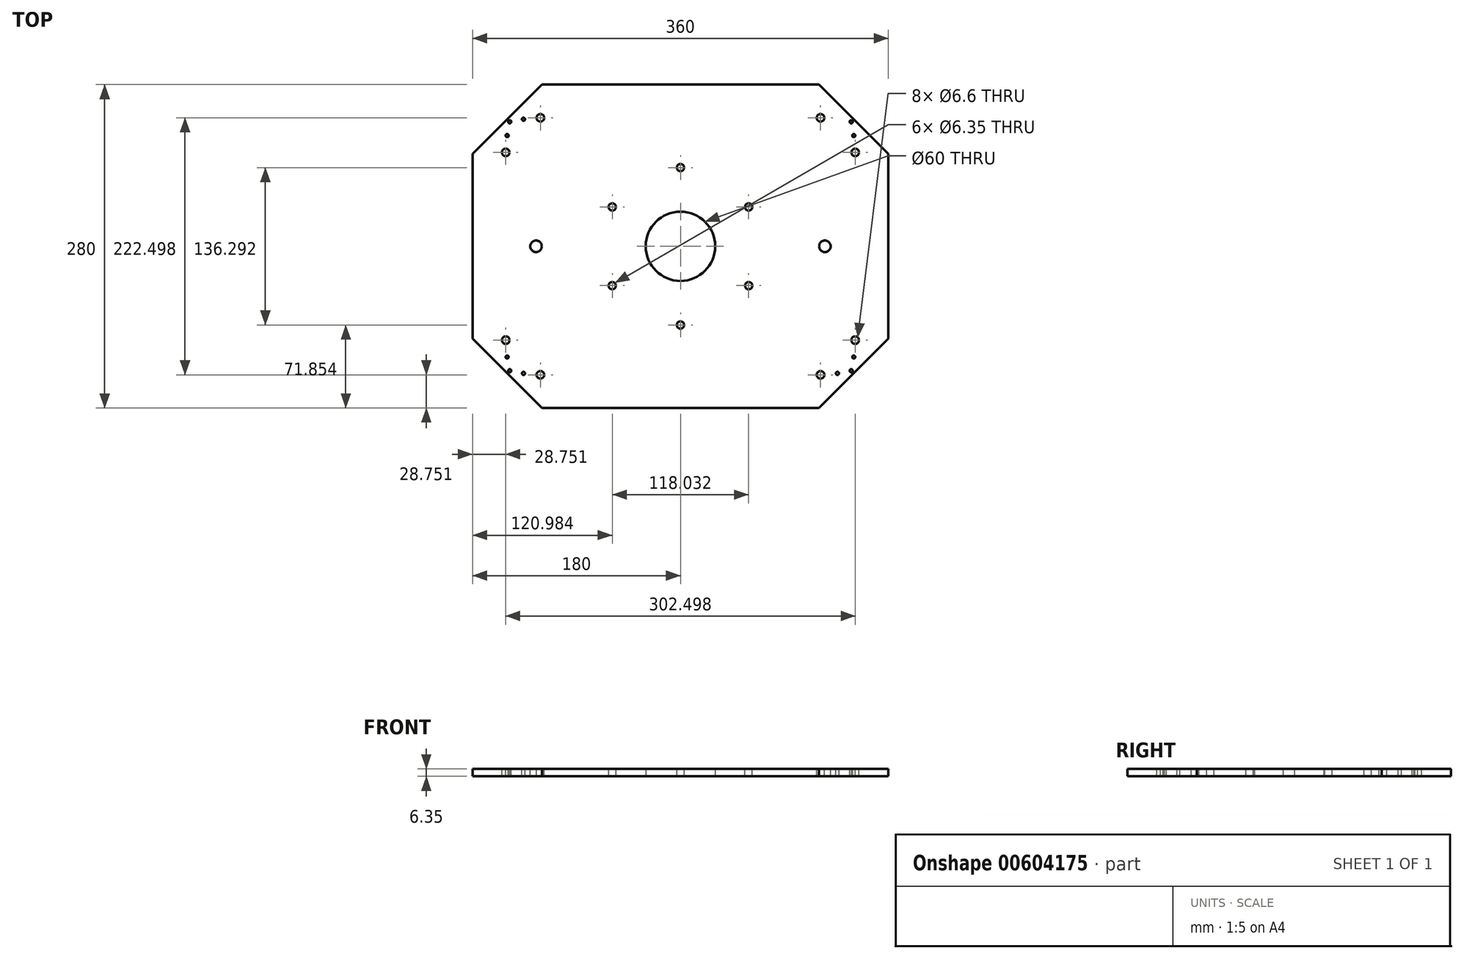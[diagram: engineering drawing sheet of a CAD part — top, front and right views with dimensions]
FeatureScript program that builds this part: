
annotation { "Feature Type Name" : "Feature", "Feature Type Description" : "" }
export const myFeature = defineFeature(function(context is Context, id is Id, definition is map)
    precondition{}
    {
        {
            var Q0;
            Q0=qCreatedBy(makeId("Top.planeOp"),FACE);
            var sketch = newSketch(context, id + "F0", { "sketchPlane" : qUnion([Q0])});
            skLineSegment(sketch, "E0", {"start": v(-120, 0) * mm, "end": v(-180, 60) * mm});
            skLineSegment(sketch, "E1", {"start": v(-180, 60) * mm, "end": v(-180, 220) * mm});
            skLineSegment(sketch, "E2", {"start": v(-180, 220) * mm, "end": v(-120, 280) * mm});
            skLineSegment(sketch, "E3", {"start": v(-120, 280) * mm, "end": v(120, 280) * mm});
            skLineSegment(sketch, "E4", {"start": v(120, 280) * mm, "end": v(180, 220) * mm});
            skLineSegment(sketch, "E5", {"start": v(180, 220) * mm, "end": v(180, 60) * mm});
            skLineSegment(sketch, "E6", {"start": v(180, 60) * mm, "end": v(120, 0) * mm});
            skLineSegment(sketch, "E7", {"start": v(120, 0) * mm, "end": v(-120, 0) * mm});
            skPoint(sketch, "E8.endSnap0", {"position": v(0, 280) * mm});
            skPoint(sketch, "E9.0.midPoint", {"position": v(0, 204.86) * mm});
            skPoint(sketch, "E10.0.midPoint", {"position": v(30.27, 157.38) * mm});
            skLineSegment(sketch, "E11", {"start": v(-180, 140) * mm, "end": v(180, 140) * mm, "construction": true});
            skLineSegment(sketch, "E12", {"start": v(0, 280) * mm, "end": v(0, 0) * mm, "construction": true});
            skCircle(sketch, "E13", {"center": v(0, 140) * mm, "radius": 30 * mm});
            skSolve(sketch);
        }
        {
            var Q0;
            Q0 = qSketchRegion(id + "F0", true);
            extrude(context, id + "F1", {"entities" : qUnion([Q0]), "depth" : 6.35 * mm, "offsetDistance" : 25 * mm});
        }
        {
            var Q0;
            {var subQ0=sQuery(id+"F0.wireOp",EDGE,"E2");var subQ1=sQuery(id+"F0.wireOp",EDGE,"E1");var subQ2=sQuery(id+"F0.wireOp",EDGE,"E3");var subQ3=sQuery(id+"F0.wireOp",EDGE,"E0");var subQ4=sQuery(id+"F0.wireOp",EDGE,"E4");var subQ5=sQuery(id+"F0.wireOp",EDGE,"E5");var subQ6=sQuery(id+"F0.wireOp",EDGE,"E6");var subQ7=sQuery(id+"F0.wireOp",EDGE,"E7");Q0=makeQuery(id+"FAH0EIdtt6uSNSP_1.boolean.opBoolean","SPLIT",FACE,{"disambiguationData":[TD([makeQuery(id+"F1.opExtrude","SWEPT_FACE",FACE,{"disambiguationData":[OSD([subQ3])]})])],"derivedFrom":makeQuery(id+"F1.opExtrude","CAP_FACE",FACE,{"disambiguationData":[OSD([subQ3,subQ1,subQ0,subQ2,subQ4,subQ5,subQ6,subQ7,sQuery(id+"F0.wireOp",EDGE,"E10.0"),sQuery(id+"F0.wireOp",EDGE,"E10.1"),sQuery(id+"F0.wireOp",EDGE,"E10.2"),sQuery(id+"F0.wireOp",EDGE,"E10.3"),sQuery(id+"F0.wireOp",EDGE,"E10.4"),sQuery(id+"F0.wireOp",EDGE,"E10.5")])],"isStart":false})});}
            var sketch = newSketch(context, id + "F2", { "sketchPlane" : qUnion([Q0])});
            skLineSegment(sketch, "E14", {"start": v(-180, 140) * mm, "end": v(180, 140) * mm, "construction": true});
            skPoint(sketch, "E15", {"position": v(0, 140) * mm});
            skPoint(sketch, "E16", {"position": v(-125, 140) * mm});
            skPoint(sketch, "E17", {"position": v(125, 140) * mm});
            skSolve(sketch);
        }
        {
            var Q0;
            Q0=sQuery(id+"F2.wireOp",VERTEX,"E16");
            var Q1;
            Q1=sQuery(id+"F2.wireOp",VERTEX,"E17");
            var Q2;
            Q2=makeQuery(id+"F1.opExtrude","SWEPT_BODY",BODY,{"disambiguationData":[OSD([sQuery(id+"F0.wireOp",EDGE,"E0"),sQuery(id+"F0.wireOp",EDGE,"E1"),sQuery(id+"F0.wireOp",EDGE,"E2"),sQuery(id+"F0.wireOp",EDGE,"E3"),sQuery(id+"F0.wireOp",EDGE,"E4"),sQuery(id+"F0.wireOp",EDGE,"E5"),sQuery(id+"F0.wireOp",EDGE,"E6"),sQuery(id+"F0.wireOp",EDGE,"E7"),sQuery(id+"F0.wireOp",EDGE,"E10.0"),sQuery(id+"F0.wireOp",EDGE,"E10.1"),sQuery(id+"F0.wireOp",EDGE,"E10.2"),sQuery(id+"F0.wireOp",EDGE,"E10.3"),sQuery(id+"F0.wireOp",EDGE,"E10.4"),sQuery(id+"F0.wireOp",EDGE,"E10.5")])]});
            hole(context, id + "F3", {"style" : HoleStyle.SIMPLE, "endStyle" : HoleEndStyle.THROUGH, "holeDiameter" : 10 * mm, "majorDiameter" : 3.17 * mm, "isTappedThrough" : true, "tappedDepth" : 12 * mm, "tapClearance" : 3, "locations" : qUnion([Q0, Q1]), "scope" : qUnion([Q2])});
        }
        {
            var Q0;
            {var subQ0=sQuery(id+"F0.wireOp",EDGE,"E2");var subQ1=sQuery(id+"F0.wireOp",EDGE,"E1");var subQ2=sQuery(id+"F0.wireOp",EDGE,"E3");var subQ3=sQuery(id+"F0.wireOp",EDGE,"E0");var subQ4=sQuery(id+"F0.wireOp",EDGE,"E4");var subQ5=sQuery(id+"F0.wireOp",EDGE,"E5");var subQ6=sQuery(id+"F0.wireOp",EDGE,"E6");var subQ7=sQuery(id+"F0.wireOp",EDGE,"E7");Q0=makeQuery(id+"FAH0EIdtt6uSNSP_1.boolean.opBoolean","SPLIT",FACE,{"disambiguationData":[TD([makeQuery(id+"F1.opExtrude","SWEPT_FACE",FACE,{"disambiguationData":[OSD([subQ3])]})])],"derivedFrom":makeQuery(id+"F1.opExtrude","CAP_FACE",FACE,{"disambiguationData":[OSD([subQ3,subQ1,subQ0,subQ2,subQ4,subQ5,subQ6,subQ7,sQuery(id+"F0.wireOp",EDGE,"E10.0"),sQuery(id+"F0.wireOp",EDGE,"E10.1"),sQuery(id+"F0.wireOp",EDGE,"E10.2"),sQuery(id+"F0.wireOp",EDGE,"E10.3"),sQuery(id+"F0.wireOp",EDGE,"E10.4"),sQuery(id+"F0.wireOp",EDGE,"E10.5")])],"isStart":false})});}
            var sketch = newSketch(context, id + "F4", { "sketchPlane" : qUnion([Q0])});
            skLineSegment(sketch, "E18", {"start": v(-150, 250) * mm, "end": v(-180, 220) * mm, "construction": true});
            skLineSegment(sketch, "E19", {"start": v(-180, 220) * mm, "end": v(-165, 235) * mm, "construction": true});
            skLineSegment(sketch, "E20", {"start": v(-165, 235) * mm, "end": v(-151.25, 221.25) * mm, "construction": true});
            skLineSegment(sketch, "E21", {"start": v(-150, 250) * mm, "end": v(-120, 280) * mm, "construction": true});
            skLineSegment(sketch, "E22", {"start": v(-120, 280) * mm, "end": v(-135, 265) * mm, "construction": true});
            skLineSegment(sketch, "E23", {"start": v(-135, 265) * mm, "end": v(-121.25, 251.25) * mm, "construction": true});
            skLineSegment(sketch, "E24", {"start": v(-150, 30) * mm, "end": v(-180, 60) * mm, "construction": true});
            skLineSegment(sketch, "E25", {"start": v(-180, 60) * mm, "end": v(-165, 45) * mm, "construction": true});
            skLineSegment(sketch, "E26", {"start": v(-165, 45) * mm, "end": v(-151.25, 58.75) * mm, "construction": true});
            skLineSegment(sketch, "E27", {"start": v(-150, 30) * mm, "end": v(-120, 0) * mm, "construction": true});
            skLineSegment(sketch, "E28", {"start": v(-120, 0) * mm, "end": v(-135, 15) * mm, "construction": true});
            skLineSegment(sketch, "E29", {"start": v(-135, 15) * mm, "end": v(-121.25, 28.75) * mm, "construction": true});
            skLineSegment(sketch, "E30", {"start": v(0, 280) * mm, "end": v(0, 0) * mm, "construction": true});
            skLineSegment(sketch, "E31.MirrorCS", {"start": v(135, 265) * mm, "end": v(121.25, 251.25) * mm, "construction": true});
            skLineSegment(sketch, "E32.MirrorCS", {"start": v(165, 235) * mm, "end": v(151.25, 221.25) * mm, "construction": true});
            skLineSegment(sketch, "E33.MirrorCS", {"start": v(165, 45) * mm, "end": v(151.25, 58.75) * mm, "construction": true});
            skLineSegment(sketch, "E34.MirrorCS", {"start": v(135, 15) * mm, "end": v(121.25, 28.75) * mm, "construction": true});
            skLineSegment(sketch, "E35", {"start": v(-180, 220) * mm, "end": v(-175.5, 215.5) * mm, "construction": true});
            skLineSegment(sketch, "E36", {"start": v(-120, 280) * mm, "end": v(-115.5, 275.5) * mm, "construction": true});
            skLineSegment(sketch, "E37", {"start": v(-142.93, 242.93) * mm, "end": v(-135.86, 250) * mm, "construction": true});
            skLineSegment(sketch, "E38", {"start": v(-142.93, 242.93) * mm, "end": v(-150, 235.86) * mm, "construction": true});
            skLineSegment(sketch, "E39.MirrorCS", {"start": v(142.93, 242.93) * mm, "end": v(150, 235.86) * mm, "construction": true});
            skLineSegment(sketch, "E40.MirrorCS", {"start": v(142.93, 242.93) * mm, "end": v(135.86, 250) * mm, "construction": true});
            skLineSegment(sketch, "E41", {"start": v(-180, 140) * mm, "end": v(180, 140) * mm, "construction": true});
            skLineSegment(sketch, "E42.MirrorCS", {"start": v(142.93, 37.07) * mm, "end": v(135.86, 30) * mm, "construction": true});
            skLineSegment(sketch, "E43.MirrorCS", {"start": v(142.93, 37.07) * mm, "end": v(150, 44.14) * mm, "construction": true});
            skLineSegment(sketch, "E44.MirrorCS", {"start": v(-142.93, 37.07) * mm, "end": v(-135.86, 30) * mm, "construction": true});
            skLineSegment(sketch, "E45.MirrorCS", {"start": v(-142.93, 37.07) * mm, "end": v(-150, 44.14) * mm, "construction": true});
            skLineSegment(sketch, "E46", {"start": v(180, 140) * mm, "end": v(180, 101.32) * mm, "construction": true});
            skLineSegment(sketch, "E47", {"start": v(180, 140) * mm, "end": v(180, 178.68) * mm, "construction": true});
            skLineSegment(sketch, "E48", {"start": v(180, 101.32) * mm, "end": v(176.82, 101.32) * mm, "construction": true});
            skLineSegment(sketch, "E49", {"start": v(180, 178.68) * mm, "end": v(176.82, 178.68) * mm, "construction": true});
            skLineSegment(sketch, "E50", {"start": v(180, 140) * mm, "end": v(180, 81.97) * mm, "construction": true});
            skLineSegment(sketch, "E51", {"start": v(180, 81.97) * mm, "end": v(176.82, 81.97) * mm, "construction": true});
            skLineSegment(sketch, "E52", {"start": v(180, 140) * mm, "end": v(180, 198.03) * mm, "construction": true});
            skLineSegment(sketch, "E53", {"start": v(180, 198.03) * mm, "end": v(176.82, 198.03) * mm, "construction": true});
            skLineSegment(sketch, "E54.MirrorCS", {"start": v(-180, 198.03) * mm, "end": v(-176.82, 198.03) * mm, "construction": true});
            skLineSegment(sketch, "E55.MirrorCS", {"start": v(-180, 178.68) * mm, "end": v(-176.82, 178.68) * mm, "construction": true});
            skLineSegment(sketch, "E56.MirrorCS", {"start": v(-180, 101.32) * mm, "end": v(-176.82, 101.32) * mm, "construction": true});
            skLineSegment(sketch, "E57.MirrorCS", {"start": v(-180, 81.97) * mm, "end": v(-176.82, 81.97) * mm, "construction": true});
            skLineSegment(sketch, "E58", {"start": v(-150, 250) * mm, "end": v(-147.75, 247.75) * mm, "construction": true});
            skLineSegment(sketch, "E59", {"start": v(-150, 30) * mm, "end": v(-147.75, 32.25) * mm, "construction": true});
            skLineSegment(sketch, "E60", {"start": v(150, 30) * mm, "end": v(147.75, 32.25) * mm, "construction": true});
            skLineSegment(sketch, "E61", {"start": v(150, 250) * mm, "end": v(147.75, 247.75) * mm, "construction": true});
            skSolve(sketch);
        }
        {
            var Q0;
            Q0=sQuery(id+"F4.wireOp",VERTEX,"E23.end");
            var Q1;
            Q1=sQuery(id+"F4.wireOp",VERTEX,"E20.end");
            var Q2;
            Q2=sQuery(id+"F4.wireOp",VERTEX,"E26.end");
            var Q3;
            Q3=sQuery(id+"F4.wireOp",VERTEX,"E29.end");
            var Q4;
            Q4=sQuery(id+"F4.wireOp",VERTEX,"E34.MirrorCS.end");
            var Q5;
            Q5=sQuery(id+"F4.wireOp",VERTEX,"E33.MirrorCS.end");
            var Q6;
            Q6=sQuery(id+"F4.wireOp",VERTEX,"E32.MirrorCS.end");
            var Q7;
            Q7=sQuery(id+"F4.wireOp",VERTEX,"E31.MirrorCS.end");
            var Q8;
            Q8=makeQuery(id+"F1.opExtrude","SWEPT_BODY",BODY,{"disambiguationData":[OSD([sQuery(id+"F0.wireOp",EDGE,"E0"),sQuery(id+"F0.wireOp",EDGE,"E1"),sQuery(id+"F0.wireOp",EDGE,"E2"),sQuery(id+"F0.wireOp",EDGE,"E3"),sQuery(id+"F0.wireOp",EDGE,"E4"),sQuery(id+"F0.wireOp",EDGE,"E5"),sQuery(id+"F0.wireOp",EDGE,"E6"),sQuery(id+"F0.wireOp",EDGE,"E7"),sQuery(id+"F0.wireOp",EDGE,"E10.0"),sQuery(id+"F0.wireOp",EDGE,"E10.1"),sQuery(id+"F0.wireOp",EDGE,"E10.2"),sQuery(id+"F0.wireOp",EDGE,"E10.3"),sQuery(id+"F0.wireOp",EDGE,"E10.4"),sQuery(id+"F0.wireOp",EDGE,"E10.5")])]});
            hole(context, id + "F5", {"style" : HoleStyle.SIMPLE, "endStyle" : HoleEndStyle.THROUGH, "standardTappedOrClearance" : lookupTablePath({ "standard" : "ISO", "fit" : "Normal", "size" : "M6", "type" : "Clearance" }), "standardBlindInLast" : lookupTablePath({ "fit" : "Standard", "standard" : "ISO", "size" : "M6", "type" : "Clearance" }), "holeDiameter" : 6.6 * mm, "majorDiameter" : 5 * mm, "isTappedThrough" : true, "tappedDepth" : 12 * mm, "tapClearance" : 3, "locations" : qUnion([Q0, Q1, Q2, Q3, Q4, Q5, Q6, Q7]), "scope" : qUnion([Q8])});
        }
        {
            var Q0;
            Q0=sQuery(id+"F4.wireOp",VERTEX,"E38.end");
            var Q1;
            Q1=sQuery(id+"F4.wireOp",VERTEX,"E37.end");
            var Q2;
            Q2=makeQuery(id+"F1.opExtrude","SWEPT_BODY",BODY,{"disambiguationData":[OSD([sQuery(id+"F0.wireOp",EDGE,"E0"),sQuery(id+"F0.wireOp",EDGE,"E1"),sQuery(id+"F0.wireOp",EDGE,"E2"),sQuery(id+"F0.wireOp",EDGE,"E3"),sQuery(id+"F0.wireOp",EDGE,"E4"),sQuery(id+"F0.wireOp",EDGE,"E5"),sQuery(id+"F0.wireOp",EDGE,"E6"),sQuery(id+"F0.wireOp",EDGE,"E7"),sQuery(id+"F0.wireOp",EDGE,"E13")])]});
            hole(context, id + "F6", {"style" : HoleStyle.SIMPLE, "endStyle" : HoleEndStyle.THROUGH, "standardTappedOrClearance" : lookupTablePath({ "standard" : "ANSI", "engagement" : "75%", "pitch" : "32 tpi", "size" : "#6", "type" : "Tapped" }), "standardBlindInLast" : lookupTablePath({ "standard" : "ANSI", "engagement" : "75%", "pitch" : "32 tpi", "size" : "#6", "type" : "Tapped" }), "holeDiameter" : 2.7 * mm, "majorDiameter" : 3.5 * mm, "showTappedDepth" : true, "isTappedThrough" : true, "tappedDepth" : 12 * mm, "tapClearance" : 3, "locations" : qUnion([Q0, Q1]), "scope" : qUnion([Q2])});
        }
        {
            var Q0;
            Q0=sQuery(id+"F4.wireOp",VERTEX,"E45.MirrorCS.end");
            var Q1;
            Q1=sQuery(id+"F4.wireOp",VERTEX,"E44.MirrorCS.end");
            var Q2;
            Q2=sQuery(id+"F4.wireOp",VERTEX,"E40.MirrorCS.end");
            var Q3;
            Q3=sQuery(id+"F4.wireOp",VERTEX,"E39.MirrorCS.end");
            var Q4;
            Q4=sQuery(id+"F4.wireOp",VERTEX,"E42.MirrorCS.end");
            var Q5;
            Q5=sQuery(id+"F4.wireOp",VERTEX,"E43.MirrorCS.end");
            var Q6;
            Q6=makeQuery(id+"F1.opExtrude","SWEPT_BODY",BODY,{"disambiguationData":[OSD([sQuery(id+"F0.wireOp",EDGE,"E0"),sQuery(id+"F0.wireOp",EDGE,"E1"),sQuery(id+"F0.wireOp",EDGE,"E2"),sQuery(id+"F0.wireOp",EDGE,"E3"),sQuery(id+"F0.wireOp",EDGE,"E4"),sQuery(id+"F0.wireOp",EDGE,"E5"),sQuery(id+"F0.wireOp",EDGE,"E6"),sQuery(id+"F0.wireOp",EDGE,"E7"),sQuery(id+"F0.wireOp",EDGE,"E13")])]});
            hole(context, id + "F7", {"style" : HoleStyle.SIMPLE, "endStyle" : HoleEndStyle.THROUGH, "standardTappedOrClearance" : lookupTablePath({ "standard" : "ANSI", "engagement" : "75%", "pitch" : "32 tpi", "size" : "#6", "type" : "Tapped" }), "standardBlindInLast" : lookupTablePath({ "standard" : "ANSI", "engagement" : "75%", "pitch" : "32 tpi", "size" : "#6", "type" : "Tapped" }), "holeDiameter" : 2.7 * mm, "majorDiameter" : 3.5 * mm, "showTappedDepth" : true, "isTappedThrough" : true, "tappedDepth" : 12 * mm, "tapClearance" : 3, "locations" : qUnion([Q0, Q1, Q2, Q3, Q4, Q5]), "scope" : qUnion([Q6])});
        }
        {
            var Q0;
            Q0=makeQuery(id+"F4.imprint","IMPRINT",FACE,{"disambiguationData":[TD([[makeQuery(id+"F4.imprint","IMPRINT",EDGE,{"derivedFrom":makeQuery(id+"F1.opExtrude","CAP_EDGE",EDGE,{"disambiguationData":[OSD([sQuery(id+"F0.wireOp",EDGE,"E0")])],"isStart":false})}),-1.0]])]});
            var sketch = newSketch(context, id + "F8", { "sketchPlane" : qUnion([Q0])});
            skCircle(sketch, "E62.cCircle", {"center": v(0, 140) * mm, "radius": 59.02 * mm, "construction": true});
            skLineSegment(sketch, "E62.0", {"start": v(0, 208.15) * mm, "end": v(59.02, 174.07) * mm});
            skLineSegment(sketch, "E62.1", {"start": v(59.02, 174.07) * mm, "end": v(59.02, 105.93) * mm});
            skLineSegment(sketch, "E62.2", {"start": v(59.02, 105.93) * mm, "end": v(0, 71.85) * mm});
            skLineSegment(sketch, "E62.3", {"start": v(0, 71.85) * mm, "end": v(-59.02, 105.93) * mm});
            skLineSegment(sketch, "E62.4", {"start": v(-59.02, 105.93) * mm, "end": v(-59.02, 174.07) * mm});
            skLineSegment(sketch, "E62.5", {"start": v(-59.02, 174.07) * mm, "end": v(0, 208.15) * mm});
            skPoint(sketch, "E62.0.midPoint", {"position": v(29.5, 191.1) * mm});
            skSolve(sketch);
        }
        {
            var Q0;
            Q0=sQuery(id+"F8.wireOp",VERTEX,"E62.5.end");
            var Q1;
            Q1=sQuery(id+"F8.wireOp",VERTEX,"E62.0.end");
            var Q2;
            Q2=sQuery(id+"F8.wireOp",VERTEX,"E62.5.start");
            var Q3;
            Q3=sQuery(id+"F8.wireOp",VERTEX,"E62.4.start");
            var Q4;
            Q4=sQuery(id+"F8.wireOp",VERTEX,"E62.2.end");
            var Q5;
            Q5=sQuery(id+"F8.wireOp",VERTEX,"E62.1.end");
            var Q6;
            Q6=makeQuery(id+"F1.opExtrude","SWEPT_BODY",BODY,{"disambiguationData":[OSD([sQuery(id+"F0.wireOp",EDGE,"E0"),sQuery(id+"F0.wireOp",EDGE,"E1"),sQuery(id+"F0.wireOp",EDGE,"E2"),sQuery(id+"F0.wireOp",EDGE,"E3"),sQuery(id+"F0.wireOp",EDGE,"E4"),sQuery(id+"F0.wireOp",EDGE,"E5"),sQuery(id+"F0.wireOp",EDGE,"E6"),sQuery(id+"F0.wireOp",EDGE,"E7"),sQuery(id+"F0.wireOp",EDGE,"E13")])]});
            hole(context, id + "F9", {"style" : HoleStyle.SIMPLE, "endStyle" : HoleEndStyle.THROUGH, "holeDiameter" : 6.35 * mm, "majorDiameter" : 3 * mm, "isTappedThrough" : true, "tappedDepth" : 12 * mm, "tapClearance" : 3, "locations" : qUnion([Q0, Q1, Q2, Q3, Q4, Q5]), "scope" : qUnion([Q6])});
        }
        {
            var Q0;
            Q0=sQuery(id+"F4.wireOp",VERTEX,"E61.end");
            var Q1;
            Q1=sQuery(id+"F4.wireOp",VERTEX,"E60.end");
            var Q2;
            Q2=sQuery(id+"F4.wireOp",VERTEX,"E59.end");
            var Q3;
            Q3=sQuery(id+"F4.wireOp",VERTEX,"E58.end");
            var Q4;
            Q4=makeQuery(id+"F1.opExtrude","SWEPT_BODY",BODY,{"disambiguationData":[OSD([sQuery(id+"F0.wireOp",EDGE,"E0"),sQuery(id+"F0.wireOp",EDGE,"E1"),sQuery(id+"F0.wireOp",EDGE,"E2"),sQuery(id+"F0.wireOp",EDGE,"E3"),sQuery(id+"F0.wireOp",EDGE,"E4"),sQuery(id+"F0.wireOp",EDGE,"E5"),sQuery(id+"F0.wireOp",EDGE,"E6"),sQuery(id+"F0.wireOp",EDGE,"E7"),sQuery(id+"F0.wireOp",EDGE,"E13")])]});
            hole(context, id + "F10", {"style" : HoleStyle.SIMPLE, "endStyle" : HoleEndStyle.THROUGH, "standardTappedOrClearance" : lookupTablePath({ "standard" : "ANSI", "engagement" : "75%", "pitch" : "32 tpi", "size" : "#6", "type" : "Tapped" }), "standardBlindInLast" : lookupTablePath({ "standard" : "ANSI", "engagement" : "75%", "pitch" : "32 tpi", "size" : "#6", "type" : "Tapped" }), "holeDiameter" : 2.7 * mm, "majorDiameter" : 3.5 * mm, "showTappedDepth" : true, "isTappedThrough" : true, "tappedDepth" : 12 * mm, "tapClearance" : 3, "locations" : qUnion([Q0, Q1, Q2, Q3]), "scope" : qUnion([Q4])});
        }
    });
